# Revit family: Pyyhekoukku
name_source: partatom
category: Casework
revit_build: Autodesk Revit 2015 (Build: 20140606_1530(x64)
units: mm (PartAtom-declared; Revit-internal decimal feet)

## types (1)
- 1907
    Depth = 56 mm  [stored 0.183727 ft]
    Height = 76 mm  [stored 0.249344 ft]
    Keynote = 1907
    Manufacturer = Korpinen Oy
    Model = Pyyhekoukku
    NominalDepth = 0 mm  [stored 0 ft]
    NominalHeight = 0 mm  [stored 0 ft]
    NominalLength = 0 mm  [stored 0 ft]
    URL = http://www.korpinen.com
    Width = 56 mm  [stored 0.183727 ft]
    var_a = 28 mm  [stored 0.0918635 ft]
    var_b = 35 mm  [stored 0.114829 ft]
    var_c = 22 mm  [stored 0.0721785 ft]
    var_d = 41 mm  [stored 0.134514 ft]
    var_e = 2 mm  [stored 0.00656168 ft]
    var_f = 5 mm  [stored 0.0164042 ft]
    var_g = 23 mm  [stored 0.0754593 ft]
    var_h = 10 mm  [stored 0.0328084 ft]

note: [stored X ft] marks values corroborated as IEEE doubles in the binary element streams (Revit-internal decimal feet)

## geometry (parser evidence)
native form markers: Sweep x2
no freeform markers — native parametric forms only
